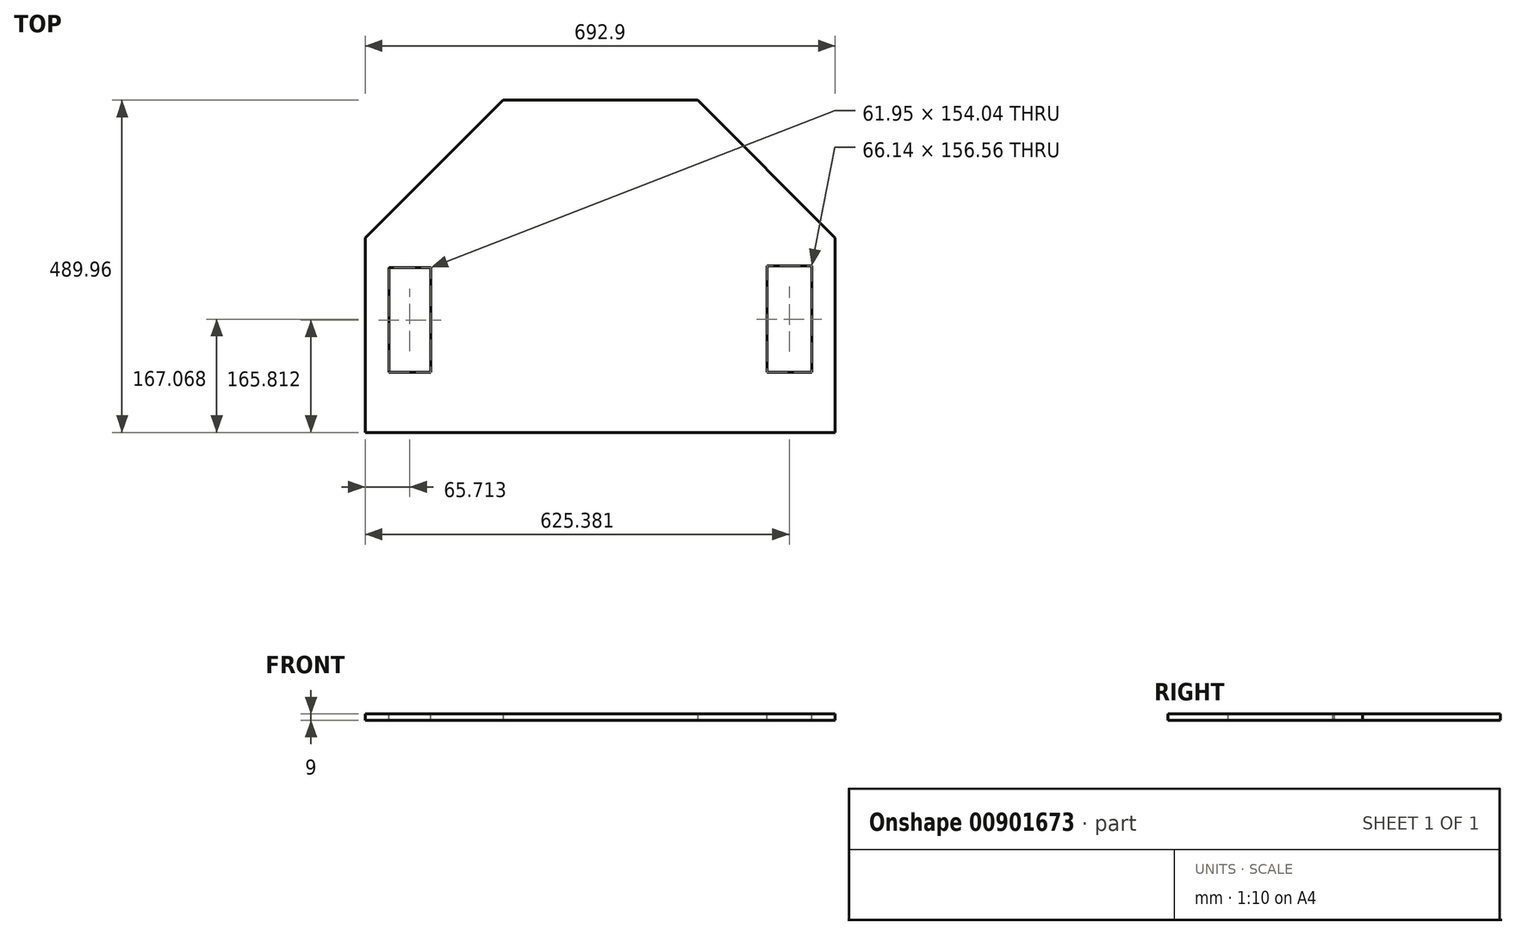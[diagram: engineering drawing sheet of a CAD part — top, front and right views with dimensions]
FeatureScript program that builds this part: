
annotation { "Feature Type Name" : "Feature", "Feature Type Description" : "" }
export const myFeature = defineFeature(function(context is Context, id is Id, definition is map)
    precondition{}
    {
        {
            var Q0;
            Q0=qCreatedBy(makeId("Top.planeOp"),FACE);
            var sketch = newSketch(context, id + "F0", { "sketchPlane" : qUnion([Q0])});
            skCircle(sketch, "E0.cCircle", {"center": v(0, 0) * mm, "radius": 375 * mm, "construction": true});
            skLineSegment(sketch, "E0.0", {"start": v(-143.5, 346.45) * mm, "end": v(143.5, 346.45) * mm});
            skLineSegment(sketch, "E0.1", {"start": v(143.5, 346.45) * mm, "end": v(346.45, 143.5) * mm});
            skLineSegment(sketch, "E0.2", {"start": v(346.45, 143.5) * mm, "end": v(346.45, -143.5) * mm});
            skLineSegment(sketch, "E0.3", {"start": v(346.45, -143.5) * mm, "end": v(143.5, -346.45) * mm});
            skLineSegment(sketch, "E0.4", {"start": v(143.5, -346.45) * mm, "end": v(-143.5, -346.45) * mm});
            skLineSegment(sketch, "E0.5", {"start": v(-143.5, -346.45) * mm, "end": v(-346.45, -143.5) * mm});
            skLineSegment(sketch, "E0.6", {"start": v(-346.45, -143.5) * mm, "end": v(-346.45, 143.5) * mm});
            skLineSegment(sketch, "E0.7", {"start": v(-346.45, 143.5) * mm, "end": v(-143.5, 346.45) * mm});
            skSolve(sketch);
        }
        {
            var Q0;
            Q0=makeQuery(id+"F0.imprint","IMPRINT",FACE,{"disambiguationData":[TD([[makeQuery(id+"F0.imprint","IMPRINT",EDGE,{"derivedFrom":sQuery(id+"F0.wireOp",EDGE,"E0.0")}),-1.0]])]});
            extrude(context, id + "F1", {"entities" : qUnion([Q0]), "depth" : 9 * mm, "offsetDistance" : 25.4 * mm});
        }
        {
            var Q0;
            Q0=makeQuery(id+"F1.opExtrude","CAP_FACE",FACE,{"disambiguationData":[OSD([sQuery(id+"F0.wireOp",EDGE,"E0.0"),sQuery(id+"F0.wireOp",EDGE,"E0.1"),sQuery(id+"F0.wireOp",EDGE,"E0.2"),sQuery(id+"F0.wireOp",EDGE,"E0.3"),sQuery(id+"F0.wireOp",EDGE,"E0.4"),sQuery(id+"F0.wireOp",EDGE,"E0.5"),sQuery(id+"F0.wireOp",EDGE,"E0.6"),sQuery(id+"F0.wireOp",EDGE,"E0.7")])],"isStart":false});
            var sketch = newSketch(context, id + "F2", { "sketchPlane" : qUnion([Q0])});
            skLineSegment(sketch, "E1", {"start": v(-346.45, -143.5) * mm, "end": v(346.45, -143.5) * mm});
            skLineSegment(sketch, "E2", {"start": v(346.45, -143.5) * mm, "end": v(143.5, -346.45) * mm});
            skLineSegment(sketch, "E3", {"start": v(143.5, -346.45) * mm, "end": v(-143.5, -346.45) * mm});
            skLineSegment(sketch, "E4", {"start": v(-143.5, -346.45) * mm, "end": v(-346.45, -143.5) * mm});
            skSolve(sketch);
        }
        {
            var Q0;
            Q0=makeQuery(id+"F2.imprint","IMPRINT",FACE,{"disambiguationData":[TD([[makeQuery(id+"F2.imprint","IMPRINT",EDGE,{"derivedFrom":sQuery(id+"F2.wireOp",EDGE,"E1")}),-1.0]])]});
            extrude(context, id + "F3", {"entities" : qUnion([Q0]), "operationType" : NewBodyOperationType.REMOVE, "endBound" : BoundingType.THROUGH_ALL, "oppositeDirection" : true, "depth" : 25 * mm, "offsetDistance" : 25 * mm});
        }
        {
            var Q0;
            Q0=makeQuery(id+"F1.opExtrude","CAP_FACE",FACE,{"disambiguationData":[OSD([sQuery(id+"F0.wireOp",EDGE,"E0.0"),sQuery(id+"F0.wireOp",EDGE,"E0.1"),sQuery(id+"F0.wireOp",EDGE,"E0.2"),sQuery(id+"F0.wireOp",EDGE,"E0.3"),sQuery(id+"F0.wireOp",EDGE,"E0.4"),sQuery(id+"F0.wireOp",EDGE,"E0.5"),sQuery(id+"F0.wireOp",EDGE,"E0.6"),sQuery(id+"F0.wireOp",EDGE,"E0.7")])],"isStart":false});
            var sketch = newSketch(context, id + "F4", { "sketchPlane" : qUnion([Q0])});
            skLineSegment(sketch, "E5.bottom", {"start": v(-311.71, 99.32) * mm, "end": v(-249.76, 99.32) * mm});
            skLineSegment(sketch, "E5.top", {"start": v(-311.71, -54.72) * mm, "end": v(-249.76, -54.72) * mm});
            skLineSegment(sketch, "E5.left", {"start": v(-311.71, 99.32) * mm, "end": v(-311.71, -54.72) * mm});
            skLineSegment(sketch, "E5.right", {"start": v(-249.76, 99.32) * mm, "end": v(-249.76, -54.72) * mm});
            skLineSegment(sketch, "E6.bottom", {"start": v(245.86, 101.84) * mm, "end": v(312, 101.84) * mm});
            skLineSegment(sketch, "E6.top", {"start": v(245.86, -54.72) * mm, "end": v(312, -54.72) * mm});
            skLineSegment(sketch, "E6.left", {"start": v(245.86, 101.84) * mm, "end": v(245.86, -54.72) * mm});
            skLineSegment(sketch, "E6.right", {"start": v(312, 101.84) * mm, "end": v(312, -54.72) * mm});
            skSolve(sketch);
        }
        {
            var Q0;
            Q0=makeQuery(id+"F4.imprint","IMPRINT",FACE,{"disambiguationData":[TD([[makeQuery(id+"F4.imprint","IMPRINT",EDGE,{"derivedFrom":sQuery(id+"F4.wireOp",EDGE,"E5.bottom")}),-1.0]])]});
            extrude(context, id + "F5", {"entities" : qUnion([Q0]), "operationType" : NewBodyOperationType.REMOVE, "endBound" : BoundingType.THROUGH_ALL, "oppositeDirection" : true, "depth" : 25 * mm, "offsetDistance" : 25 * mm});
        }
        {
            var Q0;
            Q0=makeQuery(id+"F4.imprint","IMPRINT",FACE,{"disambiguationData":[TD([[makeQuery(id+"F4.imprint","IMPRINT",EDGE,{"derivedFrom":sQuery(id+"F4.wireOp",EDGE,"E6.bottom")}),-1.0]])]});
            extrude(context, id + "F6", {"entities" : qUnion([Q0]), "operationType" : NewBodyOperationType.REMOVE, "endBound" : BoundingType.THROUGH_ALL, "oppositeDirection" : true, "depth" : 25 * mm, "offsetDistance" : 25 * mm});
        }
    });
